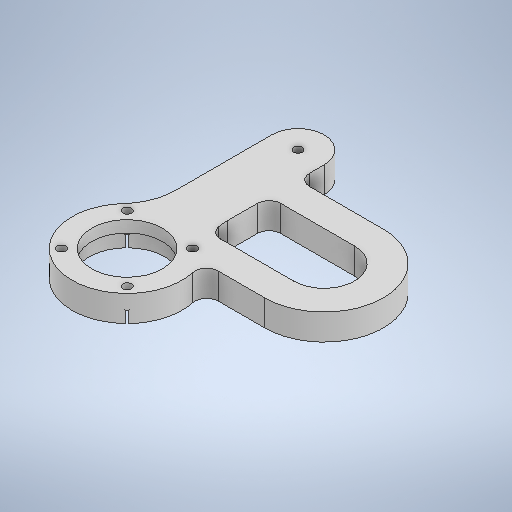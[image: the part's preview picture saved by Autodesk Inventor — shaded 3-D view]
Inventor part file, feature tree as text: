
AUTODESK INVENTOR PART (.ipt)
format: ipt  version: 2025.2 (Build 292293000, 293)  size: 738,304 bytes
history: native  units: mm
features: sketch x6, extrude x5, fillet x1, mirror x1
ambient origin geometry x8: Origin, YZ Plane, XZ Plane, XY Plane, X Axis, Y Axis, Z Axis, Center Point
bodies: Solid1 (feature_tree)
feature tree (13):
  extrude  "Extrusion1"  Depth=29.5mm
  extrude  "Extrusion2"  Depth=18.0mm
  extrude  "Extrusion3"  Depth=19.0mm
  extrude  "Extrusion4"  Depth=9.0mm
  extrude  "Extrusion5"  Depth=3.0mm
  fillet  "Fillet2"  [1 undecoded]
  mirror  "Mirror1"
  sketch  "Sketch1"  dims[d0=59.0mm d1=29.5mm]
  sketch  "Sketch2"  dims[d4=19.0mm d5=26.065mm]
  sketch  "Sketch3"  dims[d6=9.0mm d7=0.0mm d8=0.85mm]
  sketch  "Sketch4"  dims[d9=4.0mm d10=0.0mm d11=3.0mm d12=0.0mm d13=0.0mm]
  sketch  "Sketch Circular Pattern1"  dims[d2=38.0mm d3=18.0mm]
  sketch  "Sketch5"  dims[d14=45.0deg d15=3.0mm d16=40.0mm d18=360.0deg d20=0.0mm d21=0.0mm d22=6.0mm d23=6.0mm d24=6.0mm d25=6.0mm d26=4.0mm d27=0.0mm d31=10.0mm d32=59.0mm d33=4.0mm]
note: 1 required parameter value undecoded (feature->parameter linkage not recoverable at this tier; creation-order binding heuristic only, values carry confidence <= 0.55)
